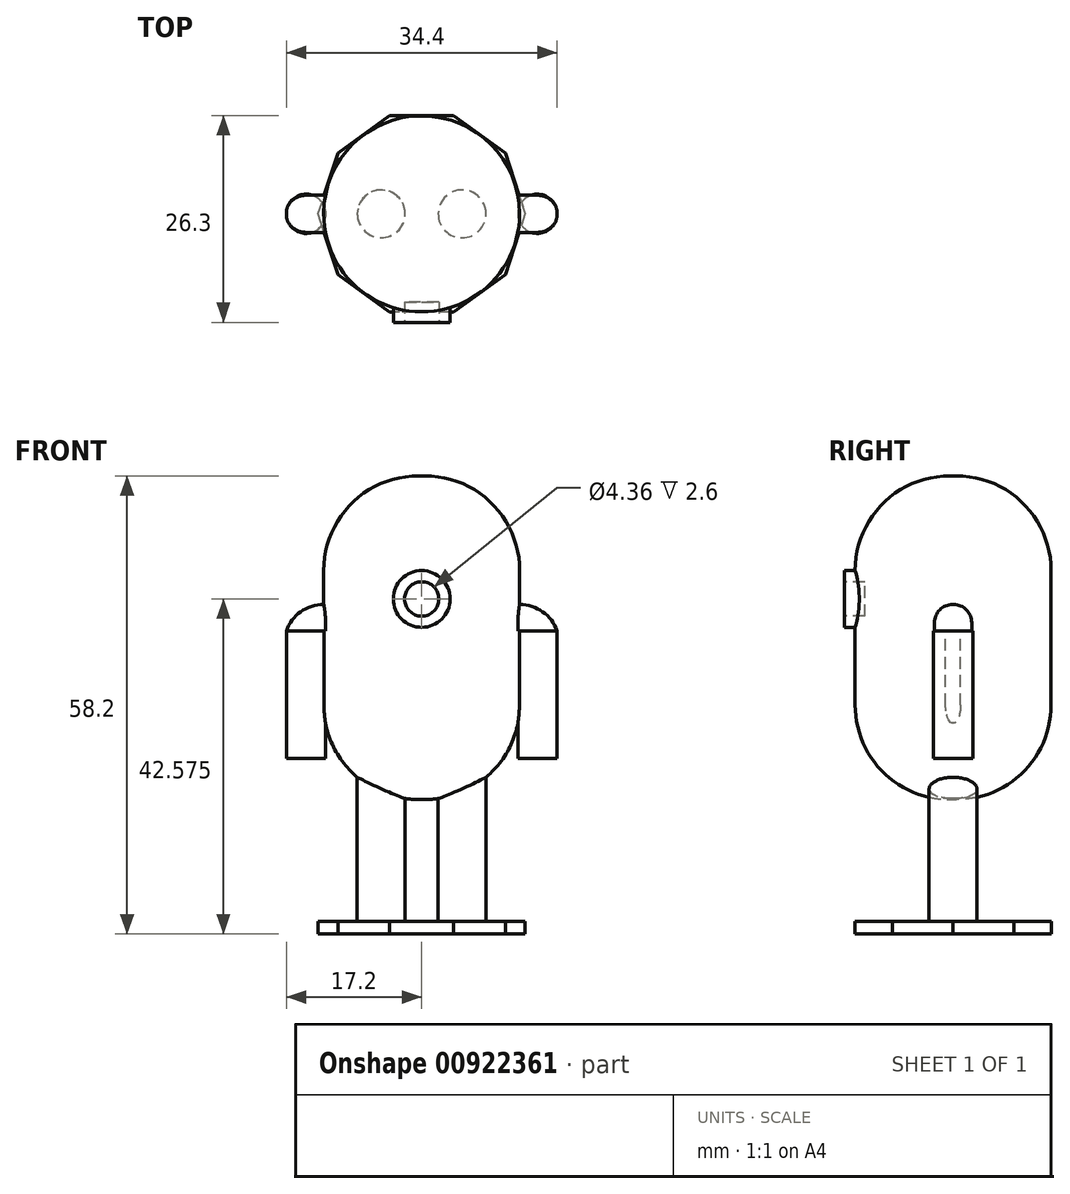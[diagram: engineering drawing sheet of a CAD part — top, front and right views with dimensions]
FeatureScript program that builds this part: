
annotation { "Feature Type Name" : "Feature", "Feature Type Description" : "" }
export const myFeature = defineFeature(function(context is Context, id is Id, definition is map)
    precondition{}
    {
        {
            var Q0;
            Q0=qCreatedBy(makeId("Top.planeOp"),FACE);
            var sketch = newSketch(context, id + "F0", { "sketchPlane" : qUnion([Q0])});
            skCircle(sketch, "E0.cCircle", {"center": v(0, 0) * mm, "radius": 12.5 * mm, "construction": true});
            skLineSegment(sketch, "E0.0", {"start": v(-4.06, 12.5) * mm, "end": v(4.06, 12.5) * mm});
            skLineSegment(sketch, "E0.1", {"start": v(4.06, 12.5) * mm, "end": v(10.63, 7.73) * mm});
            skLineSegment(sketch, "E0.2", {"start": v(10.63, 7.73) * mm, "end": v(13.14, 0) * mm});
            skLineSegment(sketch, "E0.3", {"start": v(13.14, 0) * mm, "end": v(10.63, -7.73) * mm});
            skLineSegment(sketch, "E0.4", {"start": v(10.63, -7.73) * mm, "end": v(4.06, -12.5) * mm});
            skLineSegment(sketch, "E0.5", {"start": v(4.06, -12.5) * mm, "end": v(-4.06, -12.5) * mm});
            skLineSegment(sketch, "E0.6", {"start": v(-4.06, -12.5) * mm, "end": v(-10.63, -7.73) * mm});
            skLineSegment(sketch, "E0.7", {"start": v(-10.63, -7.73) * mm, "end": v(-13.14, 0) * mm});
            skLineSegment(sketch, "E0.8", {"start": v(-13.14, 0) * mm, "end": v(-10.63, 7.73) * mm});
            skLineSegment(sketch, "E0.9", {"start": v(-10.63, 7.73) * mm, "end": v(-4.06, 12.5) * mm});
            skPoint(sketch, "E0.0.midPoint", {"position": v(0, 12.5) * mm});
            skSolve(sketch);
        }
        {
            var Q0;
            Q0 = qSketchRegion(id + "F0", true);
            extrude(context, id + "F1", {"entities" : qUnion([Q0]), "depth" : 1.6 * mm, "offsetDistance" : 25 * mm});
        }
        {
            var Q0;
            Q0=makeQuery(id+"F1.opExtrude","CAP_FACE",FACE,{"disambiguationData":[OSD([sQuery(id+"F0.wireOp",EDGE,"E0.0"),sQuery(id+"F0.wireOp",EDGE,"E0.1"),sQuery(id+"F0.wireOp",EDGE,"E0.2"),sQuery(id+"F0.wireOp",EDGE,"E0.3"),sQuery(id+"F0.wireOp",EDGE,"E0.4"),sQuery(id+"F0.wireOp",EDGE,"E0.5"),sQuery(id+"F0.wireOp",EDGE,"E0.6"),sQuery(id+"F0.wireOp",EDGE,"E0.7"),sQuery(id+"F0.wireOp",EDGE,"E0.8"),sQuery(id+"F0.wireOp",EDGE,"E0.9")])],"isStart":false});
            var sketch = newSketch(context, id + "F2", { "sketchPlane" : qUnion([Q0])});
            skCircle(sketch, "E1", {"center": v(-5.14, 0) * mm, "radius": 3.04 * mm});
            skCircle(sketch, "E2.MirrorC", {"center": v(5.14, 0) * mm, "radius": 3.04 * mm});
            skSolve(sketch);
        }
        {
            var Q0;
            Q0 = qSketchRegion(id + "F2", true);
            extrude(context, id + "F3", {"entities" : qUnion([Q0]), "operationType" : NewBodyOperationType.ADD, "depth" : 15.5 * mm, "offsetDistance" : 25 * mm});
        }
        {
            var Q0;
            Q0=makeQuery(id+"F3.opExtrude","CAP_FACE",FACE,{"disambiguationData":[OSD([sQuery(id+"F2.wireOp",EDGE,"E1")])],"isStart":false});
            var sketch = newSketch(context, id + "F4", { "sketchPlane" : qUnion([Q0])});
            skCircle(sketch, "E3", {"center": v(0, 0) * mm, "radius": 12.44 * mm});
            skSolve(sketch);
        }
        {
            var Q0;
            Q0 = qSketchRegion(id + "F4", true);
            extrude(context, id + "F5", {"entities" : qUnion([Q0]), "operationType" : NewBodyOperationType.ADD, "depth" : 41.1 * mm, "offsetDistance" : 25 * mm});
        }
        {
            var Q0;
            Q0=makeQuery(id+"F5.opExtrude","CAP_EDGE",EDGE,{"disambiguationData":[OSD([sQuery(id+"F4.wireOp",EDGE,"E3")])],"isStart":false});
            fillet(context, id + "F6", {"entities" : qUnion([Q0]), "radius" : 12 * mm, "tangentPropagation" : true, "allowEdgeOverflow" : false});
        }
        {
            var Q0;
            Q0=makeQuery(id+"F5.opExtrude","CAP_EDGE",EDGE,{"disambiguationData":[OSD([sQuery(id+"F4.wireOp",EDGE,"E3")])],"isStart":true});
            fillet(context, id + "F7", {"entities" : qUnion([Q0]), "radius" : 12 * mm, "tangentPropagation" : true, "allowEdgeOverflow" : false});
        }
        {
            var Q0;
            Q0=qCreatedBy(makeId("Right.planeOp"),FACE);
            var sketch = newSketch(context, id + "F8", { "sketchPlane" : qUnion([Q0])});
            skLineSegment(sketch, "E4.bottom", {"start": v(2.36, 38.5) * mm, "end": v(-2.36, 38.5) * mm});
            skLineSegment(sketch, "E4.top", {"start": v(2.36, 41.86) * mm, "end": v(-2.36, 41.86) * mm});
            skLineSegment(sketch, "E4.left", {"start": v(2.36, 38.5) * mm, "end": v(2.36, 41.86) * mm});
            skLineSegment(sketch, "E4.right", {"start": v(-2.36, 38.5) * mm, "end": v(-2.36, 41.86) * mm});
            skPoint(sketch, "E4.middle", {"position": v(0, 40.18) * mm});
            skSolve(sketch);
        }
        {
            var Q0;
            Q0 = qSketchRegion(id + "F8", true);
            extrude(context, id + "F9", {"entities" : qUnion([Q0]), "operationType" : NewBodyOperationType.ADD, "endBound" : BoundingType.SYMMETRIC, "depth" : 34.4 * mm, "offsetDistance" : 25 * mm});
        }
        {
            var Q0;
            {var subQ0=sQuery(id+"F8.wireOp",EDGE,"E4.left");var subQ1=sQuery(id+"F8.wireOp",EDGE,"E4.right");var subQ2=sQuery(id+"F8.wireOp",EDGE,"E4.bottom");Q0=makeQuery(id+"F9.boolean.opBoolean","SPLIT",FACE,{"disambiguationData":[TD([makeQuery(id+"F9.opExtrude","CAP_FACE",FACE,{"disambiguationData":[OSD([subQ2,sQuery(id+"F8.wireOp",EDGE,"E4.top"),subQ0,subQ1])],"isStart":false})])],"derivedFrom":makeQuery(id+"F9.opExtrude","SWEPT_FACE",FACE,{"disambiguationData":[OSD([subQ2])]})});}
            var sketch = newSketch(context, id + "F10", { "sketchPlane" : qUnion([Q0])});
            skCircle(sketch, "E5", {"center": v(14.7, 0) * mm, "radius": 2.5 * mm});
            skPoint(sketch, "E5.centerSnap0", {"position": v(14.7, -2.36) * mm});
            skPoint(sketch, "E5.centerSnap1", {"position": v(17.2, 0) * mm});
            skSolve(sketch);
        }
        {
            var Q0;
            Q0 = qSketchRegion(id + "F10", true);
            extrude(context, id + "F11", {"entities" : qUnion([Q0]), "operationType" : NewBodyOperationType.ADD, "depth" : 16.2 * mm, "offsetDistance" : 25 * mm});
        }
        {
            var Q0;
            Q0=makeQuery(id+"F1.opExtrude","SWEPT_BODY",BODY,{"disambiguationData":[OSD([sQuery(id+"F0.wireOp",EDGE,"E0.0"),sQuery(id+"F0.wireOp",EDGE,"E0.1"),sQuery(id+"F0.wireOp",EDGE,"E0.2"),sQuery(id+"F0.wireOp",EDGE,"E0.3"),sQuery(id+"F0.wireOp",EDGE,"E0.4"),sQuery(id+"F0.wireOp",EDGE,"E0.5"),sQuery(id+"F0.wireOp",EDGE,"E0.6"),sQuery(id+"F0.wireOp",EDGE,"E0.7"),sQuery(id+"F0.wireOp",EDGE,"E0.8"),sQuery(id+"F0.wireOp",EDGE,"E0.9")])]});
            var Q1;
            Q1=qCreatedBy(makeId("Right.planeOp"),FACE);
            mirror(context, id + "F12", {"operationType" : NewBodyOperationType.ADD, "entities" : qUnion([Q0]), "mirrorPlane" : qUnion([Q1])});
        }
        {
            var Q0;
            Q0=makeQuery(id+"F9.opExtrude","CAP_EDGE",EDGE,{"disambiguationData":[OSD([sQuery(id+"F8.wireOp",EDGE,"E4.top")])],"isStart":false});
            var Q1;
            Q1=makeQuery(id+"F9.opExtrude","CAP_EDGE",EDGE,{"disambiguationData":[OSD([sQuery(id+"F8.wireOp",EDGE,"E4.top")])],"isStart":true});
            fillet(context, id + "F13", {"entities" : qUnion([Q0, Q1]), "radius" : 5 * mm, "tangentPropagation" : true, "allowEdgeOverflow" : false});
        }
        {
            var Q0;
            {var subQ0=sQuery(id+"F8.wireOp",EDGE,"E4.bottom");var subQ1=sQuery(id+"F8.wireOp",EDGE,"E4.right");var subQ2=sQuery(id+"F8.wireOp",EDGE,"E4.top");Q0=makeQuery(id+"F13.opFillet","BLEND_EDGE",EDGE,{"blendedFrom":[makeQuery(id+"F9.opExtrude","CAP_EDGE",EDGE,{"disambiguationData":[OSD([subQ2])],"isStart":true}),makeQuery(id+"F9.boolean.opBoolean","SPLIT",FACE,{"disambiguationData":[TD([makeQuery(id+"F9.opExtrude","CAP_FACE",FACE,{"disambiguationData":[OSD([subQ0,subQ2,sQuery(id+"F8.wireOp",EDGE,"E4.left"),subQ1])],"isStart":true})])],"derivedFrom":makeQuery(id+"F9.opExtrude","SWEPT_FACE",FACE,{"disambiguationData":[OSD([subQ1])]})})],"blendedInto":[makeQuery(id+"F9.boolean.opBoolean","SPLIT",FACE,{"disambiguationData":[TD([makeQuery(id+"F9.opExtrude","CAP_FACE",FACE,{"disambiguationData":[OSD([subQ0,subQ2,sQuery(id+"F8.wireOp",EDGE,"E4.left"),subQ1])],"isStart":true})])],"derivedFrom":makeQuery(id+"F9.opExtrude","SWEPT_FACE",FACE,{"disambiguationData":[OSD([subQ1])]})})]});}
            var Q1;
            {var subQ0=sQuery(id+"F8.wireOp",EDGE,"E4.bottom");var subQ1=sQuery(id+"F8.wireOp",EDGE,"E4.left");var subQ2=sQuery(id+"F8.wireOp",EDGE,"E4.top");Q1=makeQuery(id+"F13.opFillet","BLEND_EDGE",EDGE,{"blendedFrom":[makeQuery(id+"F9.opExtrude","CAP_EDGE",EDGE,{"disambiguationData":[OSD([subQ2])],"isStart":true}),makeQuery(id+"F9.boolean.opBoolean","SPLIT",FACE,{"disambiguationData":[TD([makeQuery(id+"F9.opExtrude","CAP_FACE",FACE,{"disambiguationData":[OSD([subQ0,subQ2,subQ1,sQuery(id+"F8.wireOp",EDGE,"E4.right")])],"isStart":true})])],"derivedFrom":makeQuery(id+"F9.opExtrude","SWEPT_FACE",FACE,{"disambiguationData":[OSD([subQ1])]})})],"blendedInto":[makeQuery(id+"F9.boolean.opBoolean","SPLIT",FACE,{"disambiguationData":[TD([makeQuery(id+"F9.opExtrude","CAP_FACE",FACE,{"disambiguationData":[OSD([subQ0,subQ2,subQ1,sQuery(id+"F8.wireOp",EDGE,"E4.right")])],"isStart":true})])],"derivedFrom":makeQuery(id+"F9.opExtrude","SWEPT_FACE",FACE,{"disambiguationData":[OSD([subQ1])]})})]});}
            fillet(context, id + "F14", {"entities" : qUnion([Q0, Q1]), "radius" : 2.3 * mm, "tangentPropagation" : true, "allowEdgeOverflow" : false});
        }
        {
            var Q0;
            {var subQ0=sQuery(id+"F8.wireOp",EDGE,"E4.bottom");var subQ1=sQuery(id+"F8.wireOp",EDGE,"E4.right");var subQ2=sQuery(id+"F8.wireOp",EDGE,"E4.top");Q0=makeQuery(id+"F13.opFillet","BLEND_EDGE",EDGE,{"blendedFrom":[makeQuery(id+"F9.opExtrude","CAP_EDGE",EDGE,{"disambiguationData":[OSD([subQ2])],"isStart":false}),makeQuery(id+"F9.boolean.opBoolean","SPLIT",FACE,{"disambiguationData":[TD([makeQuery(id+"F9.opExtrude","CAP_FACE",FACE,{"disambiguationData":[OSD([subQ0,subQ2,sQuery(id+"F8.wireOp",EDGE,"E4.left"),subQ1])],"isStart":false})])],"derivedFrom":makeQuery(id+"F9.opExtrude","SWEPT_FACE",FACE,{"disambiguationData":[OSD([subQ1])]})})],"blendedInto":[makeQuery(id+"F9.boolean.opBoolean","SPLIT",FACE,{"disambiguationData":[TD([makeQuery(id+"F9.opExtrude","CAP_FACE",FACE,{"disambiguationData":[OSD([subQ0,subQ2,sQuery(id+"F8.wireOp",EDGE,"E4.left"),subQ1])],"isStart":false})])],"derivedFrom":makeQuery(id+"F9.opExtrude","SWEPT_FACE",FACE,{"disambiguationData":[OSD([subQ1])]})})]});}
            var Q1;
            {var subQ0=sQuery(id+"F8.wireOp",EDGE,"E4.bottom");var subQ1=sQuery(id+"F8.wireOp",EDGE,"E4.left");var subQ2=sQuery(id+"F8.wireOp",EDGE,"E4.top");Q1=makeQuery(id+"F13.opFillet","BLEND_EDGE",EDGE,{"blendedFrom":[makeQuery(id+"F9.opExtrude","CAP_EDGE",EDGE,{"disambiguationData":[OSD([subQ2])],"isStart":false}),makeQuery(id+"F9.boolean.opBoolean","SPLIT",FACE,{"disambiguationData":[TD([makeQuery(id+"F9.opExtrude","CAP_FACE",FACE,{"disambiguationData":[OSD([subQ0,subQ2,subQ1,sQuery(id+"F8.wireOp",EDGE,"E4.right")])],"isStart":false})])],"derivedFrom":makeQuery(id+"F9.opExtrude","SWEPT_FACE",FACE,{"disambiguationData":[OSD([subQ1])]})})],"blendedInto":[makeQuery(id+"F9.boolean.opBoolean","SPLIT",FACE,{"disambiguationData":[TD([makeQuery(id+"F9.opExtrude","CAP_FACE",FACE,{"disambiguationData":[OSD([subQ0,subQ2,subQ1,sQuery(id+"F8.wireOp",EDGE,"E4.right")])],"isStart":false})])],"derivedFrom":makeQuery(id+"F9.opExtrude","SWEPT_FACE",FACE,{"disambiguationData":[OSD([subQ1])]})})]});}
            fillet(context, id + "F15", {"entities" : qUnion([Q0, Q1]), "radius" : 2.3 * mm, "tangentPropagation" : true, "allowEdgeOverflow" : false});
        }
        {
            var Q0;
            Q0=qCreatedBy(makeId("Front.planeOp"),FACE);
            var sketch = newSketch(context, id + "F16", { "sketchPlane" : qUnion([Q0])});
            skCircle(sketch, "E6", {"center": v(0, 42.58) * mm, "radius": 3.6 * mm});
            skSolve(sketch);
        }
        {
            var Q0;
            Q0 = qSketchRegion(id + "F16", true);
            extrude(context, id + "F17", {"entities" : qUnion([Q0]), "operationType" : NewBodyOperationType.ADD, "depth" : 13.8 * mm, "offsetDistance" : 25 * mm});
        }
        {
            var Q0;
            Q0=makeQuery(id+"F17.opExtrude","CAP_FACE",FACE,{"disambiguationData":[OSD([sQuery(id+"F16.wireOp",EDGE,"E6")])],"isStart":false});
            var sketch = newSketch(context, id + "F18", { "sketchPlane" : qUnion([Q0])});
            skCircle(sketch, "E7", {"center": v(0, 42.58) * mm, "radius": 2.18 * mm});
            skSolve(sketch);
        }
        {
            var Q0;
            Q0 = qSketchRegion(id + "F18", true);
            extrude(context, id + "F19", {"entities" : qUnion([Q0]), "operationType" : NewBodyOperationType.REMOVE, "oppositeDirection" : true, "depth" : 2.6 * mm, "offsetDistance" : 25 * mm});
        }
    });
